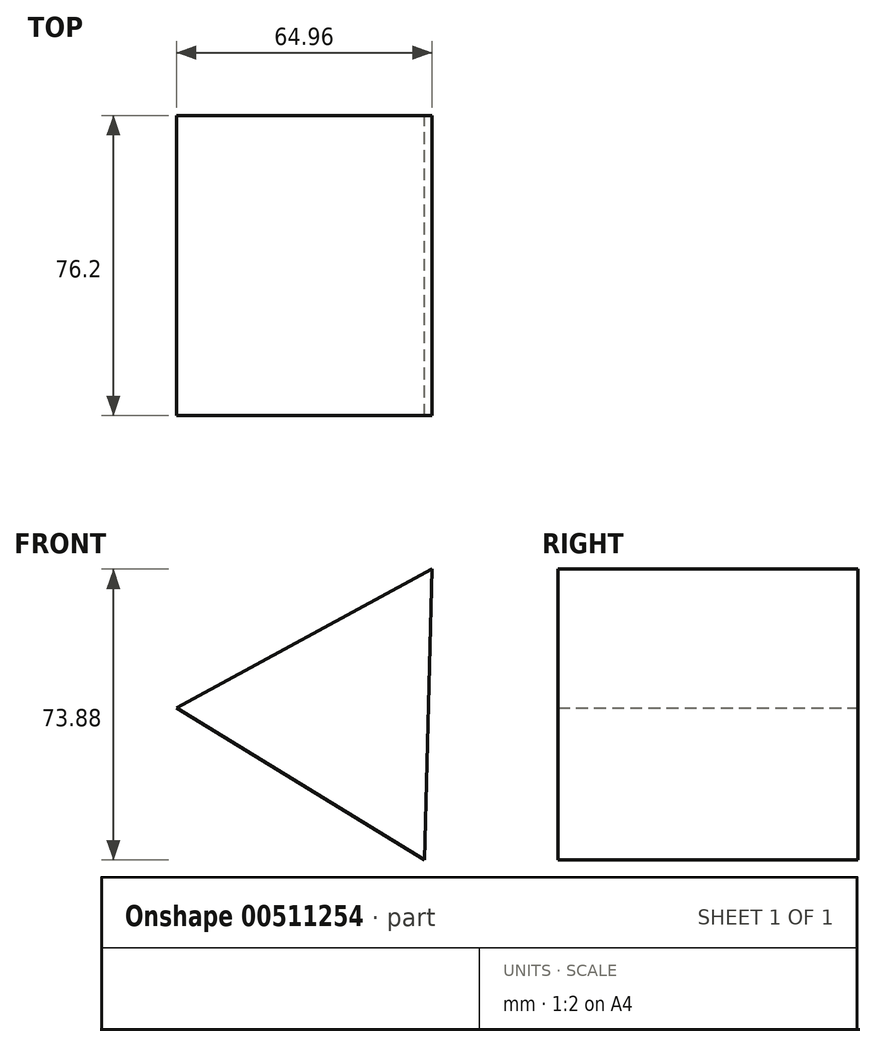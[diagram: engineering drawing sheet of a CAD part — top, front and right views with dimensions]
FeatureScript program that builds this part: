
annotation { "Feature Type Name" : "Feature", "Feature Type Description" : "" }
export const myFeature = defineFeature(function(context is Context, id is Id, definition is map)
    precondition{}
    {
        {
            var Q0;
            Q0=qCreatedBy(makeId("Front.planeOp"),FACE);
            var sketch = newSketch(context, id + "F0", { "sketchPlane" : qUnion([Q0])});
            skCircle(sketch, "E0.cCircle", {"center": v(0, 0) * mm, "radius": 42.67 * mm, "construction": true});
            skLineSegment(sketch, "E0.0", {"start": v(20.36, -37.5) * mm, "end": v(-42.66, 1.12) * mm});
            skLineSegment(sketch, "E0.1", {"start": v(-42.66, 1.12) * mm, "end": v(22.3, 36.38) * mm});
            skLineSegment(sketch, "E0.2", {"start": v(22.3, 36.38) * mm, "end": v(20.36, -37.5) * mm});
            skSolve(sketch);
        }
        {
            var Q0;
            Q0=makeQuery(id+"F0.imprint","IMPRINT",FACE,{"disambiguationData":[TD([[makeQuery(id+"F0.imprint","IMPRINT",EDGE,{"derivedFrom":sQuery(id+"F0.wireOp",EDGE,"E0.0")}),-1.0]])]});
            extrude(context, id + "F1", {"entities" : qUnion([Q0]), "depth" : 76.2 * mm});
        }
    });
